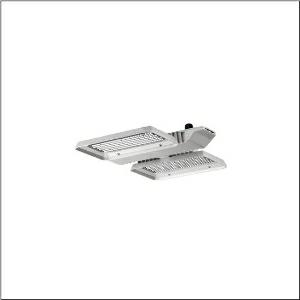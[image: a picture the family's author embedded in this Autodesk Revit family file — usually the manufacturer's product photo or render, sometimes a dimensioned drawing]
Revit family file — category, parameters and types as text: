
# Revit family: highbay_11_51hl61d14dca
name_source: partatom
category: Lighting Fixtures
units: mm (PartAtom-declared; Revit-internal decimal feet)

## family parameters
Cut with Voids When Loaded = No
Host = Face
Light Source = No
Part Type = Normal
Room Calculation Point = No
Round Connector Dimension = Use Diameter
Shared = No

## types (1)
- --- (1 x LED, 9790 lm, 55.6 W, 4000K)
    Apparent Load = 56 VA
    CIE Flux Codes = 88 95 99 100 99
    Color Rendering = 80
    Color Temperature = 4000K
    Default Elevation = 1800 mm
    Description = Highbay 11, LED high bay luminaire, primary light control with lens, of PMMA, light emission: direct distribution, primary light characteristic: symmetric, installation type: surface-mounted, suspended mounting, for 1x 2 x LED rated luminous flux: 9.790 lm, light colour: 840, colour temperature: 4000K, control gear: ECG DALI, with terminal, 5-pole, max. 2.5mm², mains connection: 230..240V, AC, 50/60Hz, rated input power: 56W, LED unit, of diecast aluminium, coated, metallic grey (RAL 9006), length: 470 mm, width: 500 mm, height: 65mm, housing, of diecast aluminium, coated, metallic grey (RAL 9006), protection rating (complete): IP65, insulation class (complete): insulation class I (protective earthing), certification: CE, ENEC, VDE, protection symbol: D, impact resistance: IK08 with glass or PC cover, permissible ambient temperature for indoor applications: -35..+70°C, corresponds to IFS (International Featured Standards) requirements for safety and quality in the food industry, reducing of maximum allowable ambient temperature of 5°C with ceiling mounting, packaging unit: 1 piece
    Height = 95 mm
    Lamp = 1 x LED
    Lamp Light Flux = 9790 lm
    Lamp Power = 55.6 W
    Lamp count = 1
    Length = 468 mm
    Luminous efficacy = 176 lm/W
    Manufacturer = Siteco
    ModVariant = No
    Model = 51HL61D14DCA
    Mounting Place = Ceiling
    Mounting Type = Pendant
    Number of Poles = 1
    OnlyDefault = Yes
    Power Factor = 1
    Product Name = Highbay 11
    Product group = LED high bay luminaire
    ProductGroupID = 903
    Protection Class = Protection class I
    Protection Degree = IP 65
    RLX_Detail_Level = 1
    RlxData = <blob elided: 70529 chars, md5=ccc547f1>
    Socket = socket
    Standby Power = 0 W
    System Light Flux = 9790 lm
    System Power = 56 W
    Type Comments = factory setting: luminous flux: 100 % | dim-lin: 254 | 315 mA
    Type Image = l_1003425.jpg
    URL = http://relux.com
    VarID = @adj_141011
    Voltage = 0 V
    Weight = 0.00 kg
    Width = 501 mm

## geometry (parser evidence)
native form markers: Blend x4, Sweep x12
no freeform markers — native parametric forms only
